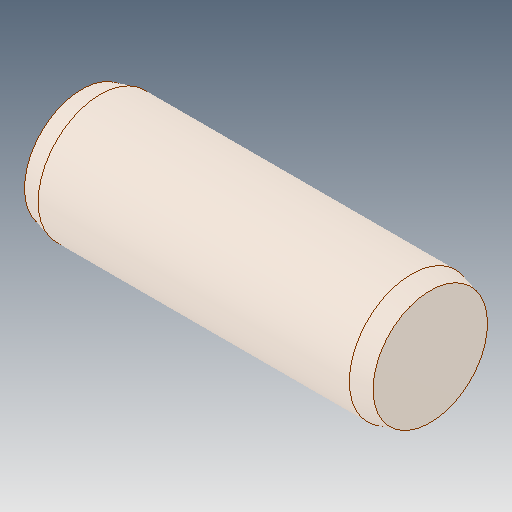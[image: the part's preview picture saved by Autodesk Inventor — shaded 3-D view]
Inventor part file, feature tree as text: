
AUTODESK INVENTOR PART (.ipt)
format: ipt  version: 2019 (Build 230136000, 136)  size: 100,864 bytes
history: native  units: mm
features: extrude x1
ambient origin geometry x8: Origin, YZ Plane, XZ Plane, XY Plane, X Axis, Y Axis, Z Axis, Center Point
bodies: Solid1 (feature_tree)
feature tree (1):
  extrude  "Extrude3"  [1 undecoded]
note: 1 required parameter value undecoded (feature->parameter linkage not recoverable at this tier; creation-order binding heuristic only, values carry confidence <= 0.55)
